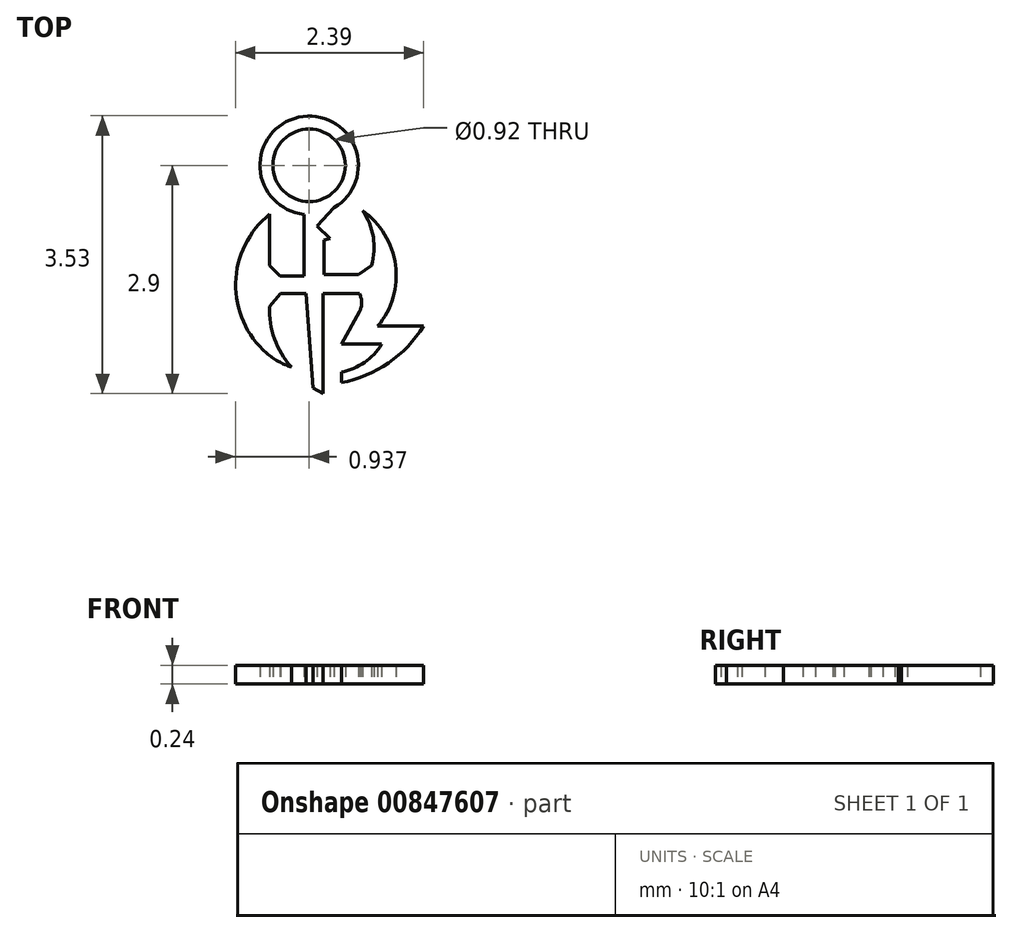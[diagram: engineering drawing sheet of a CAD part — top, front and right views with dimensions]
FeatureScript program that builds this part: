
annotation { "Feature Type Name" : "Feature", "Feature Type Description" : "" }
export const myFeature = defineFeature(function(context is Context, id is Id, definition is map)
    precondition{}
    {
        {
            var Q0;
            Q0=qCreatedBy(makeId("Top.planeOp"),FACE);
            var sketch = newSketch(context, id + "F0", { "sketchPlane" : qUnion([Q0])});
            skArc(sketch, "E0", {"start": v(-0.76, 1) * mm, "mid": v(-1.2, 0.14) * mm, "end": v(-0.8, -0.76) * mm});
            skArc(sketch, "E1", {"start": v(-0.8, -0.76) * mm, "mid": v(-0.65, -0.86) * mm, "end": v(-0.49, -0.93) * mm});
            skArc(sketch, "E2", {"start": v(-0.76, -0.16) * mm, "mid": v(-0.7, -0.57) * mm, "end": v(-0.49, -0.93) * mm});
            skLineSegment(sketch, "E3", {"start": v(-0.76, -0.16) * mm, "end": v(-0.63, 0) * mm});
            skLineSegment(sketch, "E4", {"start": v(-0.76, 1) * mm, "end": v(-0.76, 0.36) * mm});
            skLineSegment(sketch, "E5", {"start": v(-0.76, 0.36) * mm, "end": v(-0.63, 0.22) * mm});
            skLineSegment(sketch, "E6", {"start": v(-0.63, 0.22) * mm, "end": v(-0.33, 0.22) * mm});
            skLineSegment(sketch, "E7", {"start": v(-0.33, 0.22) * mm, "end": v(-0.33, 1) * mm});
            skLineSegment(sketch, "E8", {"start": v(-0.63, 0) * mm, "end": v(-0.3, 0) * mm});
            skLineSegment(sketch, "E9", {"start": v(-0.3, 0) * mm, "end": v(-0.21, -1.2) * mm});
            skLineSegment(sketch, "E10", {"start": v(-0.21, -1.2) * mm, "end": v(-0.08, -1.27) * mm});
            skLineSegment(sketch, "E11", {"start": v(-0.08, -1.27) * mm, "end": v(-0.08, 0) * mm});
            skLineSegment(sketch, "E12", {"start": v(-0.08, 0) * mm, "end": v(0.37, 0) * mm});
            skLineSegment(sketch, "E13", {"start": v(0.37, -0.23) * mm, "end": v(0.15, -0.64) * mm});
            skPoint(sketch, "E13.endSnap0", {"position": v(0.15, 0) * mm});
            skLineSegment(sketch, "E14", {"start": v(0.15, -1) * mm, "end": v(0.15, -1.13) * mm});
            skLineSegment(sketch, "E15", {"start": v(-0.08, 0.24) * mm, "end": v(-0.08, 0.68) * mm});
            skLineSegment(sketch, "E16", {"start": v(-0.33, 1) * mm, "end": v(-0.33, 1) * mm});
            skLineSegment(sketch, "E17", {"start": v(0, 0.7) * mm, "end": v(-0.08, 0.68) * mm});
            skLineSegment(sketch, "E18", {"start": v(-0.08, 0.24) * mm, "end": v(0.37, 0.24) * mm});
            skLineSegment(sketch, "E19", {"start": v(0.37, 0.24) * mm, "end": v(0.53, 0.36) * mm});
            skArc(sketch, "E20", {"start": v(0.53, 0.36) * mm, "mid": v(0.55, 0.72) * mm, "end": v(0.41, 1.05) * mm});
            skArc(sketch, "E21", {"start": v(0.6, -0.41) * mm, "mid": v(0.83, 0.36) * mm, "end": v(0.41, 1.05) * mm});
            skLineSegment(sketch, "E22", {"start": v(0.6, -0.41) * mm, "end": v(1.2, -0.41) * mm});
            skPoint(sketch, "E23.orphan", {"position": v(0.53, -0.5) * mm});
            skArc(sketch, "E24", {"start": v(0.37, -0.23) * mm, "mid": v(0.4, -0.11) * mm, "end": v(0.37, 0) * mm});
            skPoint(sketch, "E25.endSnap0", {"position": v(0.3, -0.64) * mm});
            skPoint(sketch, "E26.end.orphan", {"position": v(0.47, -0.64) * mm});
            skPoint(sketch, "E27.trimOffspring.end.orphan", {"position": v(0.53, -0.64) * mm});
            skLineSegment(sketch, "E28", {"start": v(0.15, -0.64) * mm, "end": v(0.66, -0.64) * mm});
            skArc(sketch, "E29", {"start": v(0.15, -1.13) * mm, "mid": v(0.74, -0.88) * mm, "end": v(1.2, -0.41) * mm});
            skArc(sketch, "E30", {"start": v(0.15, -1) * mm, "mid": v(0.44, -0.87) * mm, "end": v(0.66, -0.64) * mm});
            skCircle(sketch, "E31", {"center": v(-0.26, 1.63) * mm, "radius": 0.46 * mm});
            skArc(sketch, "E32", {"start": v(0.05, 1.1) * mm, "mid": v(-0.4, 2.24) * mm, "end": v(-0.33, 1) * mm});
            skLineSegment(sketch, "E33", {"start": v(-0.16, 0.86) * mm, "end": v(0.05, 1.1) * mm});
            skLineSegment(sketch, "E34.trimOffspring", {"start": v(-0.16, 0.86) * mm, "end": v(0, 0.7) * mm});
            skSolve(sketch);
        }
        {
            var Q0;
            Q0 = qSketchRegion(id + "F0", true);
            extrude(context, id + "F1", {"entities" : qUnion([Q0]), "depth" : 0.24 * mm, "offsetDistance" : 25 * mm});
        }
    });
